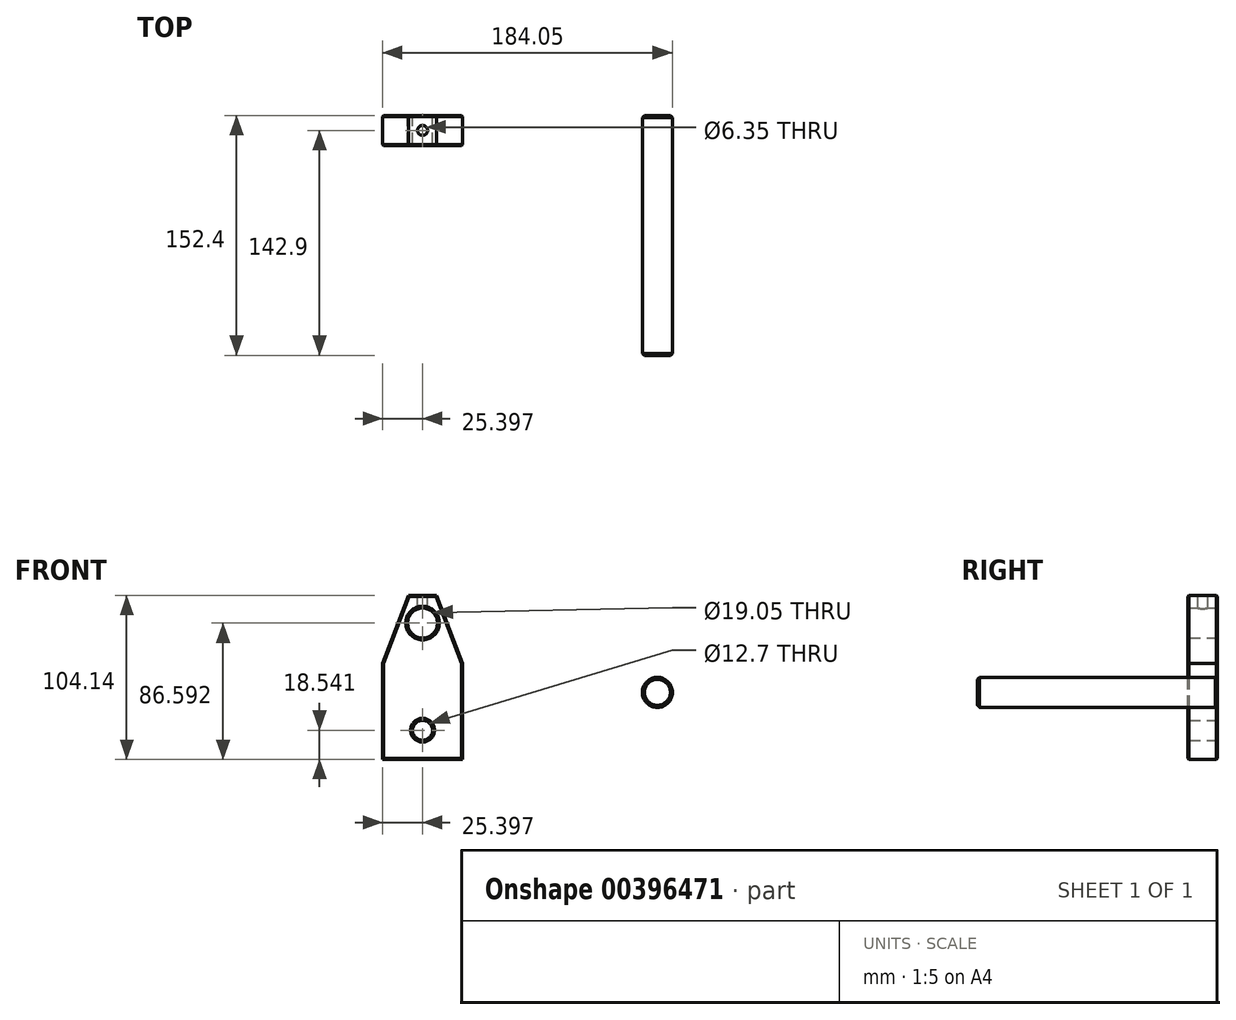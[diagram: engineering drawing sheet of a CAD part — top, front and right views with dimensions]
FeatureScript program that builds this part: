
annotation { "Feature Type Name" : "Feature", "Feature Type Description" : "" }
export const myFeature = defineFeature(function(context is Context, id is Id, definition is map)
    precondition{}
    {
        {
            var Q0;
            Q0=qCreatedBy(makeId("Front.planeOp"),FACE);
            var sketch = newSketch(context, id + "F0", { "sketchPlane" : qUnion([Q0])});
            skCircle(sketch, "E0", {"center": v(0, 0) * mm, "radius": 9.52 * mm});
            skSolve(sketch);
        }
        {
            var Q0;
            Q0=makeQuery(id+"F0.imprint","IMPRINT",FACE,{"disambiguationData":[TD([[makeQuery(id+"F0.imprint","IMPRINT",EDGE,{"derivedFrom":sQuery(id+"F0.wireOp",EDGE,"E0")}),1.0]])]});
            extrude(context, id + "F1", {"entities" : qUnion([Q0]), "depth" : 152.4 * mm});
        }
        {
            var Q0;
            Q0=makeQuery(id+"F1.opExtrude","CAP_FACE",FACE,{"disambiguationData":[OSD([sQuery(id+"F0.wireOp",EDGE,"E0")])],"isStart":false});
            var Q1;
            Q1=makeQuery(id+"F1.opExtrude","CAP_EDGE",EDGE,{"disambiguationData":[OSD([sQuery(id+"F0.wireOp",EDGE,"E0")])],"isStart":true});
            chamfer(context, id + "F2", {"entities" : qUnion([Q0, Q1]), "width" : 1.27 * mm, "tangentPropagation" : true});
        }
        {
            var Q0;
            Q0=qCreatedBy(makeId("Front.planeOp"),FACE);
            var sketch = newSketch(context, id + "F3", { "sketchPlane" : qUnion([Q0])});
            skLineSegment(sketch, "E1", {"start": v(-123.72, -42.6) * mm, "end": v(-174.52, -42.6) * mm});
            skLineSegment(sketch, "E2", {"start": v(-174.52, -42.6) * mm, "end": v(-174.52, 18.36) * mm});
            skLineSegment(sketch, "E3", {"start": v(-158.01, 61.54) * mm, "end": v(-140.23, 61.54) * mm});
            skLineSegment(sketch, "E4", {"start": v(-123.72, 18.36) * mm, "end": v(-123.72, -42.6) * mm});
            skLineSegment(sketch, "E5", {"start": v(-140.23, 61.54) * mm, "end": v(-123.72, 18.36) * mm});
            skLineSegment(sketch, "E6", {"start": v(-174.52, 18.36) * mm, "end": v(-158.01, 61.54) * mm});
            skPoint(sketch, "E7.orphan", {"position": v(-123.72, 61.54) * mm});
            skPoint(sketch, "E8.endSnap0", {"position": v(-131.98, 39.95) * mm});
            skCircle(sketch, "E9", {"center": v(-149.12, 44) * mm, "radius": 9.53 * mm});
            skPoint(sketch, "E10.orphan", {"position": v(-149.12, 61.54) * mm});
            skLineSegment(sketch, "E11.trimOffspring", {"start": v(-133.52, 44) * mm, "end": v(-131.98, 44) * mm});
            skCircle(sketch, "E12", {"center": v(-149.12, -24.06) * mm, "radius": 6.35 * mm});
            skPoint(sketch, "E13.orphan", {"position": v(-149.12, -42.6) * mm});
            skSolve(sketch);
        }
        {
            var Q0;
            Q0=makeQuery(id+"F3.imprint","IMPRINT",FACE,{"disambiguationData":[TD([[makeQuery(id+"F3.imprint","IMPRINT",EDGE,{"derivedFrom":sQuery(id+"F3.wireOp",EDGE,"E1")}),-1.0]])]});
            extrude(context, id + "F4", {"entities" : qUnion([Q0]), "depth" : 19 * mm});
        }
        {
            var Q0;
            Q0=makeQuery(id+"F4.opExtrude","SWEPT_FACE",FACE,{"disambiguationData":[OSD([sQuery(id+"F3.wireOp",EDGE,"E3")])]});
            var sketch = newSketch(context, id + "F5", { "sketchPlane" : qUnion([Q0])});
            skCircle(sketch, "E14", {"center": v(-149.12, -9.5) * mm, "radius": 3.18 * mm});
            skPoint(sketch, "E15.orphan", {"position": v(-149.12, 0) * mm});
            skPoint(sketch, "E16.trimOffspring.end.orphan", {"position": v(-140.23, -9.5) * mm});
            skPoint(sketch, "E17.start.orphan", {"position": v(-149.12, -19) * mm});
            skPoint(sketch, "E18.start.orphan", {"position": v(-158.01, -9.5) * mm});
            skSolve(sketch);
        }
        {
            var Q0;
            Q0=makeQuery(id+"F5.imprint","IMPRINT",FACE,{"disambiguationData":[TD([[makeQuery(id+"F5.imprint","IMPRINT",EDGE,{"derivedFrom":sQuery(id+"F5.wireOp",EDGE,"E14")}),1.0]])]});
            extrude(context, id + "F6", {"entities" : qUnion([Q0]), "operationType" : NewBodyOperationType.REMOVE, "oppositeDirection" : true, "depth" : 19.3 * mm});
        }
        {
            var Q0;
            Q0=makeQuery(id+"F4.opExtrude","CAP_FACE",FACE,{"disambiguationData":[OSD([sQuery(id+"F3.wireOp",EDGE,"E1"),sQuery(id+"F3.wireOp",EDGE,"E2"),sQuery(id+"F3.wireOp",EDGE,"E3"),sQuery(id+"F3.wireOp",EDGE,"E4"),sQuery(id+"F3.wireOp",EDGE,"E5"),sQuery(id+"F3.wireOp",EDGE,"E6"),sQuery(id+"F3.wireOp",EDGE,"E9"),sQuery(id+"F3.wireOp",EDGE,"E12")])],"isStart":false});
            var Q1;
            Q1=makeQuery(id+"F4.opExtrude","CAP_FACE",FACE,{"disambiguationData":[OSD([sQuery(id+"F3.wireOp",EDGE,"E1"),sQuery(id+"F3.wireOp",EDGE,"E2"),sQuery(id+"F3.wireOp",EDGE,"E3"),sQuery(id+"F3.wireOp",EDGE,"E4"),sQuery(id+"F3.wireOp",EDGE,"E5"),sQuery(id+"F3.wireOp",EDGE,"E6"),sQuery(id+"F3.wireOp",EDGE,"E9"),sQuery(id+"F3.wireOp",EDGE,"E12")])],"isStart":true});
            chamfer(context, id + "F7", {"entities" : qUnion([Q0, Q1]), "width" : 0.64 * mm, "tangentPropagation" : true});
        }
        {
            var Q0;
            {var subQ0=sQuery(id+"F3.wireOp",EDGE,"E12");Q0=makeQuery(id+"F7.opChamfer","BLEND_EDGE",EDGE,{"blendedFrom":[makeQuery(id+"F4.opExtrude","CAP_EDGE",EDGE,{"disambiguationData":[OSD([subQ0])],"isStart":false}),makeQuery(id+"F4.opExtrude","CAP_FACE",FACE,{"disambiguationData":[OSD([sQuery(id+"F3.wireOp",EDGE,"E1"),sQuery(id+"F3.wireOp",EDGE,"E2"),sQuery(id+"F3.wireOp",EDGE,"E3"),sQuery(id+"F3.wireOp",EDGE,"E4"),sQuery(id+"F3.wireOp",EDGE,"E5"),sQuery(id+"F3.wireOp",EDGE,"E6"),sQuery(id+"F3.wireOp",EDGE,"E9"),subQ0])],"isStart":false})],"blendedInto":[makeQuery(id+"F4.opExtrude","CAP_FACE",FACE,{"disambiguationData":[OSD([sQuery(id+"F3.wireOp",EDGE,"E1"),sQuery(id+"F3.wireOp",EDGE,"E2"),sQuery(id+"F3.wireOp",EDGE,"E3"),sQuery(id+"F3.wireOp",EDGE,"E4"),sQuery(id+"F3.wireOp",EDGE,"E5"),sQuery(id+"F3.wireOp",EDGE,"E6"),sQuery(id+"F3.wireOp",EDGE,"E9"),subQ0])],"isStart":false})]});}
            var Q1;
            {var subQ0=sQuery(id+"F3.wireOp",EDGE,"E9");Q1=makeQuery(id+"F7.opChamfer","BLEND_EDGE",EDGE,{"blendedFrom":[makeQuery(id+"F4.opExtrude","CAP_EDGE",EDGE,{"disambiguationData":[OSD([subQ0])],"isStart":false}),makeQuery(id+"F4.opExtrude","CAP_FACE",FACE,{"disambiguationData":[OSD([sQuery(id+"F3.wireOp",EDGE,"E1"),sQuery(id+"F3.wireOp",EDGE,"E2"),sQuery(id+"F3.wireOp",EDGE,"E3"),sQuery(id+"F3.wireOp",EDGE,"E4"),sQuery(id+"F3.wireOp",EDGE,"E5"),sQuery(id+"F3.wireOp",EDGE,"E6"),subQ0,sQuery(id+"F3.wireOp",EDGE,"E12")])],"isStart":false})],"blendedInto":[makeQuery(id+"F4.opExtrude","CAP_FACE",FACE,{"disambiguationData":[OSD([sQuery(id+"F3.wireOp",EDGE,"E1"),sQuery(id+"F3.wireOp",EDGE,"E2"),sQuery(id+"F3.wireOp",EDGE,"E3"),sQuery(id+"F3.wireOp",EDGE,"E4"),sQuery(id+"F3.wireOp",EDGE,"E5"),sQuery(id+"F3.wireOp",EDGE,"E6"),subQ0,sQuery(id+"F3.wireOp",EDGE,"E12")])],"isStart":false})]});}
            var Q2;
            {var subQ0=sQuery(id+"F3.wireOp",EDGE,"E9");Q2=makeQuery(id+"F7.opChamfer","BLEND_EDGE",EDGE,{"blendedFrom":[makeQuery(id+"F4.opExtrude","CAP_EDGE",EDGE,{"disambiguationData":[OSD([subQ0])],"isStart":true}),makeQuery(id+"F4.opExtrude","CAP_FACE",FACE,{"disambiguationData":[OSD([sQuery(id+"F3.wireOp",EDGE,"E1"),sQuery(id+"F3.wireOp",EDGE,"E2"),sQuery(id+"F3.wireOp",EDGE,"E3"),sQuery(id+"F3.wireOp",EDGE,"E4"),sQuery(id+"F3.wireOp",EDGE,"E5"),sQuery(id+"F3.wireOp",EDGE,"E6"),subQ0,sQuery(id+"F3.wireOp",EDGE,"E12")])],"isStart":true})],"blendedInto":[makeQuery(id+"F4.opExtrude","CAP_FACE",FACE,{"disambiguationData":[OSD([sQuery(id+"F3.wireOp",EDGE,"E1"),sQuery(id+"F3.wireOp",EDGE,"E2"),sQuery(id+"F3.wireOp",EDGE,"E3"),sQuery(id+"F3.wireOp",EDGE,"E4"),sQuery(id+"F3.wireOp",EDGE,"E5"),sQuery(id+"F3.wireOp",EDGE,"E6"),subQ0,sQuery(id+"F3.wireOp",EDGE,"E12")])],"isStart":true})]});}
            var Q3;
            {var subQ0=sQuery(id+"F3.wireOp",EDGE,"E12");Q3=makeQuery(id+"F7.opChamfer","BLEND_EDGE",EDGE,{"blendedFrom":[makeQuery(id+"F4.opExtrude","CAP_EDGE",EDGE,{"disambiguationData":[OSD([subQ0])],"isStart":true}),makeQuery(id+"F4.opExtrude","CAP_FACE",FACE,{"disambiguationData":[OSD([sQuery(id+"F3.wireOp",EDGE,"E1"),sQuery(id+"F3.wireOp",EDGE,"E2"),sQuery(id+"F3.wireOp",EDGE,"E3"),sQuery(id+"F3.wireOp",EDGE,"E4"),sQuery(id+"F3.wireOp",EDGE,"E5"),sQuery(id+"F3.wireOp",EDGE,"E6"),sQuery(id+"F3.wireOp",EDGE,"E9"),subQ0])],"isStart":true})],"blendedInto":[makeQuery(id+"F4.opExtrude","CAP_FACE",FACE,{"disambiguationData":[OSD([sQuery(id+"F3.wireOp",EDGE,"E1"),sQuery(id+"F3.wireOp",EDGE,"E2"),sQuery(id+"F3.wireOp",EDGE,"E3"),sQuery(id+"F3.wireOp",EDGE,"E4"),sQuery(id+"F3.wireOp",EDGE,"E5"),sQuery(id+"F3.wireOp",EDGE,"E6"),sQuery(id+"F3.wireOp",EDGE,"E9"),subQ0])],"isStart":true})]});}
            var Q4;
            Q4=makeQuery(id+"F6.boolean.opBoolean","COPY",EDGE,{"derivedFrom":makeQuery(id+"F6.opExtrude","CAP_EDGE",EDGE,{"disambiguationData":[OSD([sQuery(id+"F5.wireOp",EDGE,"E14")])],"isStart":true})});
            chamfer(context, id + "F8", {"entities" : qUnion([Q0, Q1, Q2, Q3, Q4]), "width" : 1.27 * mm, "tangentPropagation" : true});
        }
    });
